# Revit family: CS-152_001CP
name_source: partatom
category: Plumbing Fixtures
revit_build: Autodesk Revit Architecture 2012 (Build: 20110309_2315(x64)
units: mm (PartAtom-declared; Revit-internal decimal feet)

## types (1)
- CS-152/001CP
    3/4" tap washer = C-097-20
    Assembly Code = D2010
    CW Connection = Yes
    CWFU = 0
    Cost = 0 $
    Default Elevation = 0' - 0"
    Description = Pillar type with diverter and handshower attachment. 3/4"BSP male inlets
    HW Connection = Yes
    HWFU = 0
    Handshower = VIC-001/1CP
    Handshower cradle = VIC-CRADLE
    Handshower hose = 008/4C
    Headpart complete = P-91-2CSS
    Keynote = 3/4" low resistance for low pressure or high water demand installations
    Manufacturer = COBRA
    Material = Chrome - Polished
    Model = CS-152/001CP
    Range = Capstan
    Type Comments = SANS 226 TYPE 1
    URL = http://www.cobra.co.za
    Vent Connection = No
    WFU = 0
    Waste Connection = No

## geometry (parser evidence)
native form markers: Blend x2
no freeform markers — native parametric forms only
